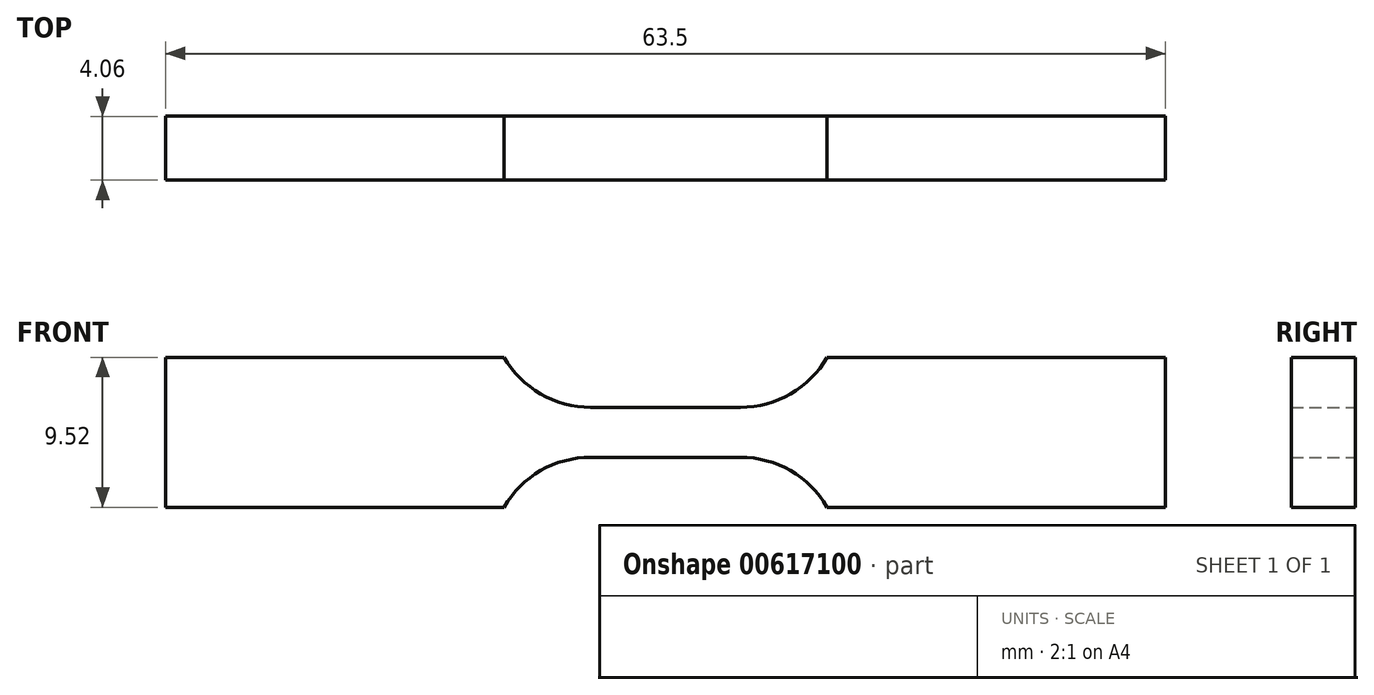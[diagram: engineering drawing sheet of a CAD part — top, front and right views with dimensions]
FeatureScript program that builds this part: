
annotation { "Feature Type Name" : "Feature", "Feature Type Description" : "" }
export const myFeature = defineFeature(function(context is Context, id is Id, definition is map)
    precondition{}
    {
        {
            var Q0;
            Q0=qCreatedBy(makeId("Front.planeOp"),FACE);
            var sketch = newSketch(context, id + "F0", { "sketchPlane" : qUnion([Q0])});
            skLineSegment(sketch, "E0", {"start": v(-31.75, 4.76) * mm, "end": v(-31.75, 0) * mm});
            skLineSegment(sketch, "E1", {"start": v(-31.75, -4.76) * mm, "end": v(-10.26, -4.76) * mm});
            skLineSegment(sketch, "E2", {"start": v(-31.75, 4.76) * mm, "end": v(-10.26, 4.76) * mm});
            skLineSegment(sketch, "E3", {"start": v(10.26, -4.76) * mm, "end": v(31.75, -4.76) * mm});
            skLineSegment(sketch, "E4", {"start": v(31.75, -4.76) * mm, "end": v(31.75, 0) * mm});
            skLineSegment(sketch, "E5", {"start": v(31.75, 4.76) * mm, "end": v(10.26, 4.76) * mm});
            skLineSegment(sketch, "E6", {"start": v(-4.76, 1.59) * mm, "end": v(0, 1.59) * mm});
            skLineSegment(sketch, "E7", {"start": v(-4.76, -1.59) * mm, "end": v(0, -1.59) * mm});
            skArc(sketch, "E8", {"start": v(-10.26, 4.76) * mm, "mid": v(-7.94, 2.44) * mm, "end": v(-4.76, 1.59) * mm});
            skArc(sketch, "E9", {"start": v(-4.76, -1.59) * mm, "mid": v(-7.94, -2.44) * mm, "end": v(-10.26, -4.76) * mm});
            skArc(sketch, "E10", {"start": v(10.26, -4.76) * mm, "mid": v(7.94, -2.44) * mm, "end": v(4.76, -1.59) * mm});
            skArc(sketch, "E11", {"start": v(4.76, 1.59) * mm, "mid": v(7.94, 2.44) * mm, "end": v(10.26, 4.76) * mm});
            skLineSegment(sketch, "E12", {"start": v(-31.75, 0) * mm, "end": v(-31.75, -4.76) * mm});
            skLineSegment(sketch, "E13", {"start": v(31.75, 0) * mm, "end": v(31.75, 4.76) * mm});
            skLineSegment(sketch, "E14", {"start": v(0, 1.59) * mm, "end": v(4.76, 1.59) * mm});
            skLineSegment(sketch, "E15", {"start": v(0, -1.59) * mm, "end": v(4.76, -1.59) * mm});
            skSolve(sketch);
        }
        {
            var Q0;
            Q0 = qSketchRegion(id + "F0", true);
            extrude(context, id + "F1", {"entities" : qUnion([Q0]), "endBound" : BoundingType.SYMMETRIC, "depth" : 4.06 * mm, "offsetDistance" : 25.4 * mm});
        }
    });
